# Revit family: Wash_Fountain -One,Two_Station-(3401-ES_3402-ES)_Series
name_source: partatom
category: Plumbing Fixtures
units: mm (PartAtom-declared; Revit-internal decimal feet)

## family parameters
Cut with Voids When Loaded = No
Host = Face
OmniClass Number = 23.45.05.14.14
OmniClass Title = Sinks/Lavatories
Part Type = Normal
Room Calculation Point = No
Round Connector Dimension = Use Diameter
Shared = Yes

## types (2) — shared parameters
-1 Off-Floor, Wall Outlet, ADA Compliant OPERATION (Must Specify) = Yes
-EG Enviro-Glaze Color, Bowl and Sprayhead Specify ______________ = No
-H Hand Operation = No
-HB Hose Bibb, Specify ,Left Side or Right Side = No
-PPZ Programmable Piezo button Electronic Metering = No
-SO Sensor Operation = No
-SO-BAT Sensor Operation (Batteries Not Included) = No
-ST Single Temperature Valve = No
ADA Compliant = Yes
Assembly Code = D2010600
CW Connection = Yes
CWFU = 2
Compliance Certifications = Sensor and handoperated units conform to ANSI, UFAS and ADA requirements for accessibility
Default Elevation = 34"
Description = One Station, Elliptical Wash Fountain with Contour Base
Finish = Stainless Steel-Acorn-Satin
Flow Rate = 0.5 GPM
HW Connection = Yes
HWFU = 2
Height = 22 1/2"
Inlet Connection Diameter = 1/2"
Installation Type = Wall Mounted
Length = 27 3/4"
Manufacturer = Acorn
Material = Stainless Steel-Acorn-Satin
Product Documentation Link = https://www.acorneng.com
Product Page URL = https://www.acorneng.com
Tempered Water Connection = No
URL = https://www.acorneng.com
Vent Connection = No
WFU = 3
Waste Connection = Yes
Waste Connection Diameter = 1 1/2"
Width = 17 1/4"

## per-type parameters (varying)
| type | 3401-ES Elliptical with Contoured Base, One Station | 3402-ES Elliptical with Contoured Base, Two Station | Type Comments |
| 3401-ES | Yes | No | Elliptical with Contoured Base, One Station |
| 3402-ES | No | Yes | Elliptical with Contoured Base, Two Station |

note: column(s) folded — value = type name in every type: Model

## geometry (parser evidence)
native form markers: Sweep x3
no freeform markers — native parametric forms only
